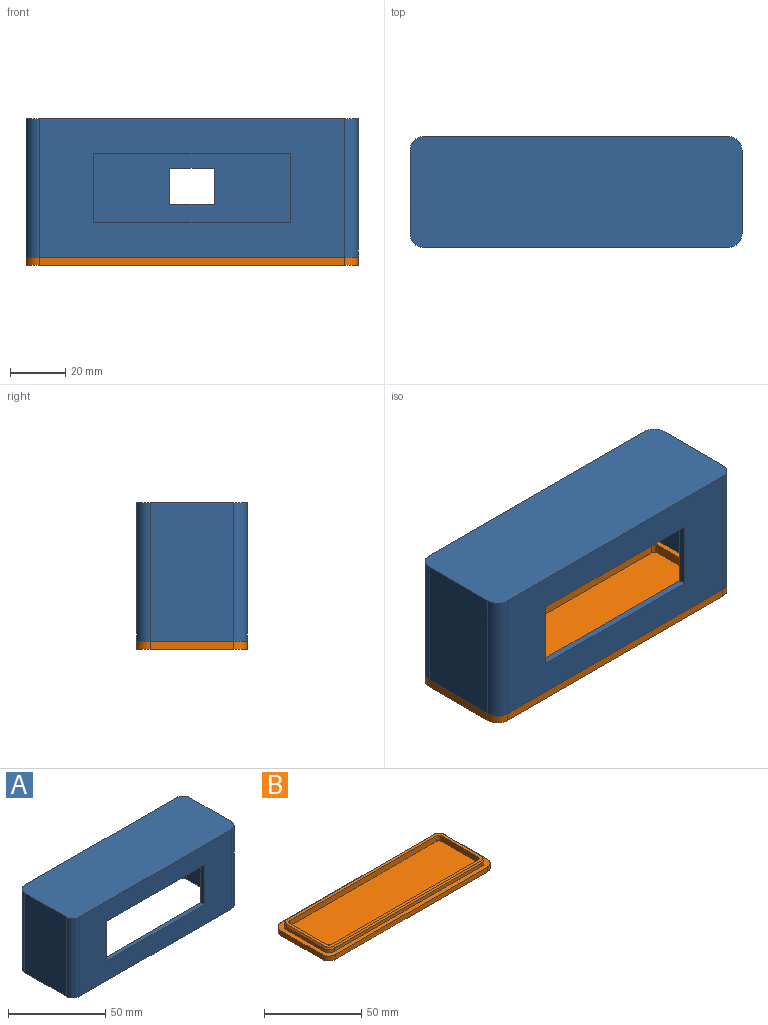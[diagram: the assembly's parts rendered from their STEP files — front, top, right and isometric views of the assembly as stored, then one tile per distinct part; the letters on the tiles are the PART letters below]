
ASSEMBLY  parts=2 mates=1
PART A: 31 faces, bbox 120x40x50 mm
  f0: plane 50x30mm, normal (1,0,0), area 1468mm2, adj f4,f7,f9,f10,f23,f24,f25,f26
  f1: plane 47.5x30mm, normal (-1,0,0), area 1393mm2, adj f4,f14,f16,f17,f23,f24,f25,f26
  f2: plane 110x50mm, normal (0,-1,0), area 3725mm2, adj f4,f7,f8,f9,f19,f20,f21,f22
  f3: plane 110x47.5mm, normal (0,1,0), area 3450mm2, adj f4,f14,f15,f16,f19,f20,f21,f22
  f4: plane 120x40mm, normal (0,0,-1), area 758.9mm2, adj f0,f1,f2,f3,f5,f6,f8,f9
  f5: plane 50x30mm, normal (-1,0,0), area 1500mm2, adj f4,f7,f8,f11
  f6: plane 110x50mm, normal (0,1,0), area 5292mm2, adj f4,f7,f10,f11,f27,f28,f29,f30
  f7: plane 120x40mm, normal (0,0,1), area 4778.5mm2, adj f0,f2,f5,f6,f8,f9,f10,f11
  f8: cylinder r=5mm len=50mm, axis (0,0,1), area 392.7mm2, adj f2,f4,f5,f7
  f9: cylinder r=5mm len=50mm, axis (0,0,-1), area 392.7mm2, adj f0,f2,f4,f7
  f10: cylinder r=5mm len=50mm, axis (0,0,1), area 392.7mm2, adj f0,f4,f6,f7
  f11: cylinder r=5mm len=50mm, axis (0,0,-1), area 392.7mm2, adj f4,f5,f6,f7
  f12: plane 47.5x30mm, normal (1,0,0), area 1425mm2, adj f4,f14,f15,f18
  f13: plane 110x47.5mm, normal (0,-1,0), area 5017mm2, adj f4,f14,f17,f18,f27,f28,f29,f30
  f14: plane 115x35mm, normal (0,0,-1), area 4019.6mm2, adj f1,f3,f12,f13,f15,f16,f17,f18
  f15: cylinder r=2.5mm len=47.5mm, axis (0,0,1), area 186.5mm2, adj f3,f4,f12,f14
  f16: cylinder r=2.5mm len=47.5mm, axis (0,0,-1), area 186.5mm2, adj f1,f3,f4,f14
  f17: cylinder r=2.5mm len=47.5mm, axis (0,0,1), area 186.5mm2, adj f1,f4,f13,f14
  f18: cylinder r=2.5mm len=47.5mm, axis (0,0,-1), area 186.5mm2, adj f4,f12,f13,f14
  f19: plane 71x2.5mm, normal (0,0,-1), area 177.5mm2, adj f2,f3,f20,f22
  f20: plane 25x2.5mm, normal (1,0,0), area 62.5mm2, adj f2,f3,f19,f21
  f21: plane 71x2.5mm, normal (0,0,1), area 177.5mm2, adj f2,f3,f20,f22
  f22: plane 25x2.5mm, normal (-1,0,0), area 62.5mm2, adj f2,f3,f19,f21
  f23: plane 4x2.5mm, normal (0,0,-1), area 10mm2, adj f0,f1,f24,f26
  f24: plane 8x2.5mm, normal (0,1,0), area 20mm2, adj f0,f1,f23,f25
  f25: plane 4x2.5mm, normal (0,0,1), area 10mm2, adj f0,f1,f24,f26
  f26: plane 8x2.5mm, normal (0,-1,0), area 20mm2, adj f0,f1,f23,f25
  f27: plane 13x2.5mm, normal (-1,0,0), area 32.5mm2, adj f6,f13,f28,f29
  f28: plane 16x2.5mm, normal (0,0,-1), area 40mm2, adj f6,f13,f27,f30
  f29: plane 16x2.5mm, normal (0,0,1), area 40mm2, adj f6,f13,f27,f30
  f30: plane 13x2.5mm, normal (1,0,0), area 32.5mm2, adj f6,f13,f28,f29
PART B: 36 faces, bbox 120x40x6 mm
  f0: plane 113.85x33.85mm, normal (0,0,1), area 545mm2, adj f15,f16,f17,f18,f19,f20,f21,f22
  f1: plane 120x40mm, normal (0,0,1), area 767.3mm2, adj f2,f3,f4,f5,f7,f8,f9,f10
  f2: plane 110x3mm, normal (0,-1,0), area 330mm2, adj f1,f6,f32,f35
  f3: plane 30x3mm, normal (-1,0,0), area 90mm2, adj f1,f6,f32,f33
  f4: plane 110x3mm, normal (0,1,0), area 330mm2, adj f1,f6,f33,f34
  f5: plane 30x3mm, normal (1,0,0), area 90mm2, adj f1,f6,f34,f35
  f6: plane 120x40mm, normal (0,0,-1), area 4778.5mm2, adj f2,f3,f4,f5,f32,f33,f34,f35
  f7: plane 107x2mm, normal (0,-1,0), area 214mm2, adj f1,f11,f14,f25
  f8: plane 27x2mm, normal (-1,0,0), area 54mm2, adj f1,f11,f12,f26
  f9: plane 107x2mm, normal (0,1,0), area 214mm2, adj f1,f12,f13,f30
  f10: plane 27x2mm, normal (1,0,0), area 54mm2, adj f1,f13,f14,f29
  f11: cylinder r=4mm len=4mm, axis (0,0,1), area 12.6mm2, adj f1,f7,f8,f24
  f12: cylinder r=4mm len=4mm, axis (0,0,-1), area 12.6mm2, adj f1,f8,f9,f28
  f13: cylinder r=4mm len=4mm, axis (0,0,1), area 12.6mm2, adj f1,f9,f10,f31
  f14: cylinder r=4mm len=4mm, axis (0,0,-1), area 12.6mm2, adj f1,f7,f10,f27
  f15: cylinder r=1.5mm len=3.5mm, axis (0,0,-1), area 8.2mm2, adj f0,f16,f22,f23
  f16: plane 27x3.5mm, normal (-1,0,0), area 94.5mm2, adj f0,f15,f17,f23
  f17: cylinder r=1.5mm len=3.5mm, axis (0,0,1), area 8.2mm2, adj f0,f16,f18,f23
  f18: plane 107x3.5mm, normal (0,-1,0), area 374.5mm2, adj f0,f17,f19,f23
  f19: cylinder r=1.5mm len=3.5mm, axis (0,0,-1), area 8.2mm2, adj f0,f18,f20,f23
  f20: plane 27x3.5mm, normal (1,0,0), area 94.5mm2, adj f0,f19,f21,f23
  f21: cylinder r=1.5mm len=3.5mm, axis (0,0,1), area 8.2mm2, adj f0,f20,f22,f23
  f22: plane 107x3.5mm, normal (0,1,0), area 374.5mm2, adj f0,f15,f21,f23
  f23: plane 110x30mm, normal (0,0,1), area 3298.1mm2, adj f15,f16,f17,f18,f19,f20,f21,f22
  f24: cone r=3.42mm half-angle=30deg, axis (0,0,-1), area 6.7mm2, adj f0,f11,f25,f26
  f25: plane 107x1mm, normal (0,-0.87,0.5), area 123.6mm2, adj f0,f7,f24,f27
  f26: plane 27x1mm, normal (-0.87,0,0.5), area 31.2mm2, adj f0,f8,f24,f28
  f27: cone r=3.42mm half-angle=30deg, axis (0,0,-1), area 6.7mm2, adj f0,f14,f25,f29
  f28: cone r=3.42mm half-angle=30deg, axis (0,0,-1), area 6.7mm2, adj f0,f12,f26,f30
  f29: plane 27x1mm, normal (0.87,0,0.5), area 31.2mm2, adj f0,f10,f27,f31
  f30: plane 107x1mm, normal (0,0.87,0.5), area 123.6mm2, adj f0,f9,f28,f31
  f31: cone r=3.42mm half-angle=30deg, axis (0,0,-1), area 6.7mm2, adj f0,f13,f29,f30
  f32: cylinder r=5mm len=5mm, axis (0,0,-1), area 23.6mm2, adj f1,f2,f3,f6
  f33: cylinder r=5mm len=5mm, axis (0,0,1), area 23.6mm2, adj f1,f3,f4,f6
  f34: cylinder r=5mm len=5mm, axis (0,0,-1), area 23.6mm2, adj f1,f4,f5,f6
  f35: cylinder r=5mm len=5mm, axis (0,0,1), area 23.6mm2, adj f1,f2,f5,f6
PLACE A at identity
PLACE B at identity
MATE planar B.f7 <-> A.f3  axis (0,-1,0) through (60,2.5,1)mm
